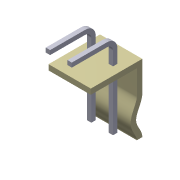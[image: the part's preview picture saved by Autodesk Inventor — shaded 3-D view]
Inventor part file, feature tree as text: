
AUTODESK INVENTOR PART (.ipt)
format: ipt  version: 2015 SP1 (Build 190203100, 203)  size: 156,160 bytes
history: native  units: mm
features: sketch x4, other x3, sweep x2, projected_geometry x2
ambient origin geometry x8: Origin, YZ Plane, XZ Plane, XY Plane, X Axis, Y Axis, Z Axis, Center Point
bodies: Body1 (feature_tree)
feature tree (11):
  other  "Твердое тело1"
  sketch  "Эскиз1"
  other  "РабПлоскость1"
  other  "РабПлоскость2"
  sweep  "Сдвиг1"
  sweep  "Сдвиг2"
  sketch  "Эскиз4"
  sketch  "Эскиз2"
  sketch  "Эскиз3"
  projected_geometry  "Спроецированная петля1"
  projected_geometry  "Спроецированная петля2"
